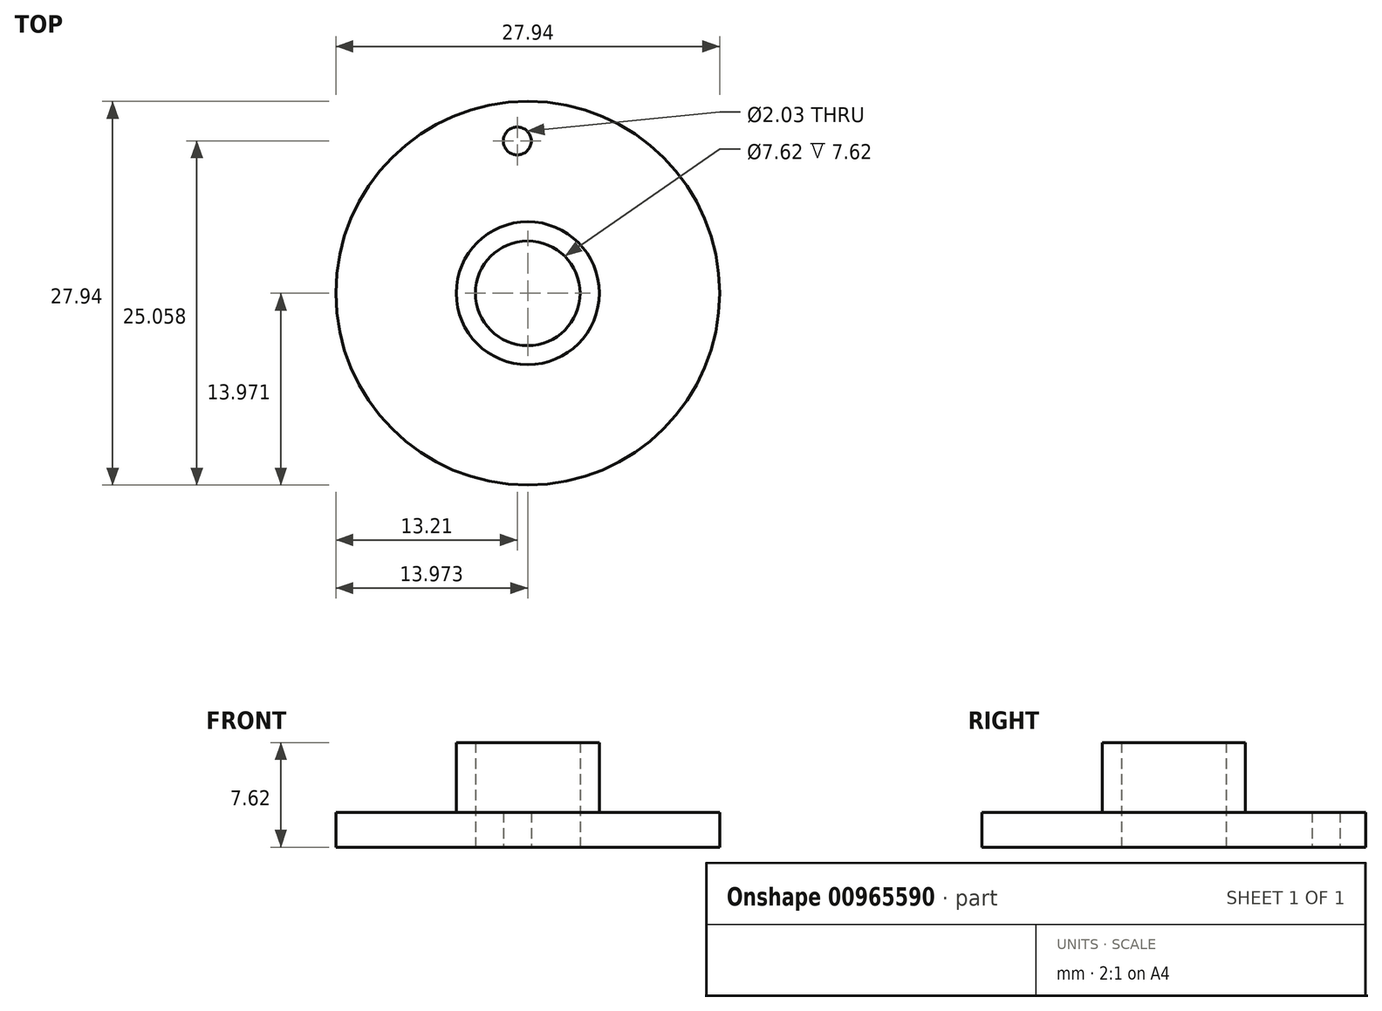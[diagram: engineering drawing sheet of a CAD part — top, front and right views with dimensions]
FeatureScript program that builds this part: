
annotation { "Feature Type Name" : "Feature", "Feature Type Description" : "" }
export const myFeature = defineFeature(function(context is Context, id is Id, definition is map)
    precondition{}
    {
        {
            var Q0;
            Q0=qCreatedBy(makeId("Top.planeOp"),FACE);
            var sketch = newSketch(context, id + "F0", { "sketchPlane" : qUnion([Q0])});
            skCircle(sketch, "E0", {"center": v(-56.14, 35.7) * mm, "radius": 13.97 * mm});
            skCircle(sketch, "E1", {"center": v(-56.14, 35.7) * mm, "radius": 5.2 * mm});
            skCircle(sketch, "E2", {"center": v(-56.9, 46.78) * mm, "radius": 1.02 * mm});
            skCircle(sketch, "E3", {"center": v(-56.14, 35.7) * mm, "radius": 3.81 * mm});
            skSolve(sketch);
        }
        {
            var Q0;
            Q0 = qSketchRegion(id + "F0", true);
            extrude(context, id + "F1", {"entities" : qUnion([Q0]), "depth" : 2.54 * mm, "offsetDistance" : 25.4 * mm});
        }
        {
            var Q0;
            Q0=makeQuery(id+"F0.imprint","IMPRINT",FACE,{"disambiguationData":[TD([[makeQuery(id+"F0.imprint","IMPRINT",EDGE,{"derivedFrom":sQuery(id+"F0.wireOp",EDGE,"E1")}),1.0]])]});
            extrude(context, id + "F2", {"entities" : qUnion([Q0]), "operationType" : NewBodyOperationType.ADD, "depth" : 7.62 * mm, "offsetDistance" : 25.4 * mm});
        }
    });
